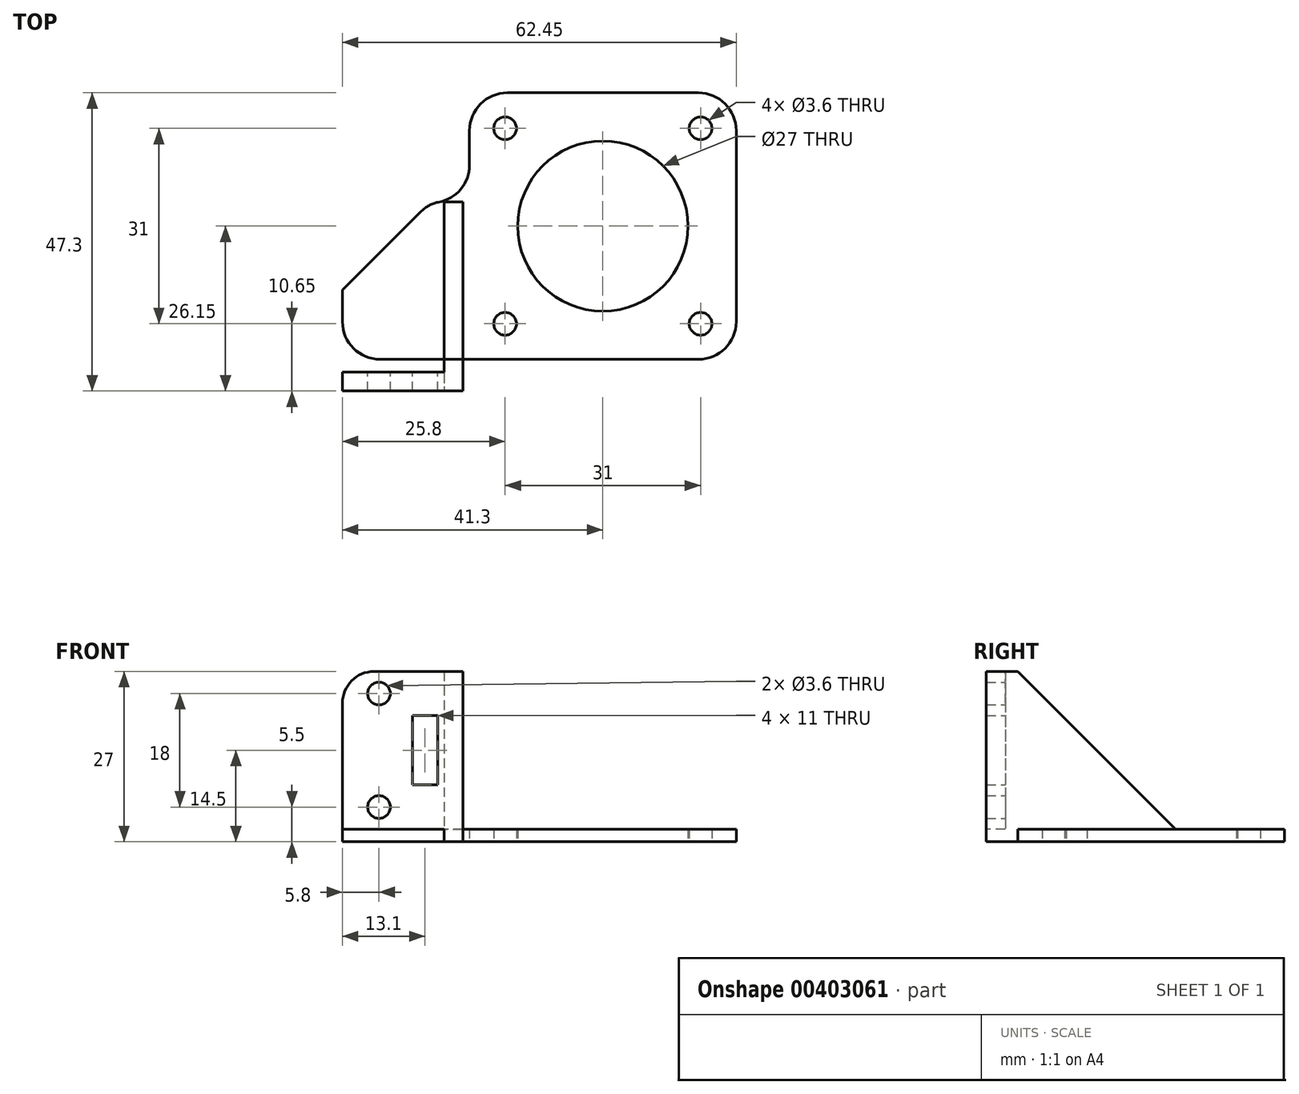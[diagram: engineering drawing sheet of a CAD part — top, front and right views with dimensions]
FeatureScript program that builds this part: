
annotation { "Feature Type Name" : "Feature", "Feature Type Description" : "" }
export const myFeature = defineFeature(function(context is Context, id is Id, definition is map)
    precondition{}
    {
        {
            var Q0;
            Q0=qCreatedBy(makeId("Top.planeOp"),FACE);
            var sketch = newSketch(context, id + "F0", { "sketchPlane" : qUnion([Q0])});
            skLineSegment(sketch, "E0.bottom", {"start": v(21.15, 21.15) * mm, "end": v(-21.15, 21.15) * mm});
            skLineSegment(sketch, "E0.top", {"start": v(21.15, -21.15) * mm, "end": v(-21.15, -21.15) * mm});
            skLineSegment(sketch, "E0.left", {"start": v(21.15, 21.15) * mm, "end": v(21.15, -21.15) * mm});
            skLineSegment(sketch, "E0.right", {"start": v(-21.15, 21.15) * mm, "end": v(-21.15, -21.15) * mm});
            skPoint(sketch, "E0.middle", {"position": v(0, 0) * mm});
            skLineSegment(sketch, "E1.bottom", {"start": v(15.5, 15.5) * mm, "end": v(-15.5, 15.5) * mm, "construction": true});
            skLineSegment(sketch, "E1.top", {"start": v(15.5, -15.5) * mm, "end": v(-15.5, -15.5) * mm, "construction": true});
            skLineSegment(sketch, "E1.left", {"start": v(15.5, 15.5) * mm, "end": v(15.5, -15.5) * mm, "construction": true});
            skLineSegment(sketch, "E1.right", {"start": v(-15.5, 15.5) * mm, "end": v(-15.5, -15.5) * mm, "construction": true});
            skCircle(sketch, "E2", {"center": v(-15.5, 15.5) * mm, "radius": 1.8 * mm});
            skCircle(sketch, "E3", {"center": v(15.5, 15.5) * mm, "radius": 1.8 * mm});
            skCircle(sketch, "E4", {"center": v(15.5, -15.5) * mm, "radius": 1.8 * mm});
            skCircle(sketch, "E5", {"center": v(-15.5, -15.5) * mm, "radius": 1.8 * mm});
            skCircle(sketch, "E6", {"center": v(0, 0) * mm, "radius": 13.5 * mm});
            skLineSegment(sketch, "E7.bottom", {"start": v(-21.15, -21.15) * mm, "end": v(-41.3, -21.15) * mm});
            skLineSegment(sketch, "E7.top", {"start": v(-21.15, 3.85) * mm, "end": v(-41.3, 3.85) * mm});
            skLineSegment(sketch, "E7.left", {"start": v(-21.15, -21.15) * mm, "end": v(-21.15, 3.85) * mm});
            skLineSegment(sketch, "E7.right", {"start": v(-41.3, -21.15) * mm, "end": v(-41.3, 3.85) * mm});
            skLineSegment(sketch, "E8.bottom", {"start": v(-41.3, -21.15) * mm, "end": v(-21.16, -21.15) * mm});
            skLineSegment(sketch, "E8.top", {"start": v(-41.3, -26.15) * mm, "end": v(-21.16, -26.15) * mm});
            skLineSegment(sketch, "E8.left", {"start": v(-41.3, -21.15) * mm, "end": v(-41.3, -26.15) * mm});
            skLineSegment(sketch, "E8.right", {"start": v(-21.16, -21.15) * mm, "end": v(-21.16, -26.15) * mm});
            skSolve(sketch);
        }
        {
            var Q0;
            Q0=makeQuery(id+"F0.imprint","IMPRINT",FACE,{"disambiguationData":[TD([[makeQuery(id+"F0.imprint","IMPRINT",EDGE,{"derivedFrom":sQuery(id+"F0.wireOp",EDGE,"E0.bottom")}),1.0]])]});
            var Q1;
            Q1=makeQuery(id+"F0.imprint","IMPRINT",FACE,{"disambiguationData":[TD([[makeQuery(id+"F0.imprint","IMPRINT",EDGE,{"derivedFrom":sQuery(id+"F0.wireOp",EDGE,"E7.bottom")}),-1.0]])]});
            var Q2;
            Q2=makeQuery(id+"F0.imprint","IMPRINT",FACE,{"disambiguationData":[TD([[makeQuery(id+"F0.imprint","IMPRINT",EDGE,{"derivedFrom":sQuery(id+"F0.wireOp",EDGE,"E8.bottom")}),-1.0]])]});
            extrude(context, id + "F1", {"entities" : qUnion([Q0, Q1, Q2]), "depth" : 2 * mm});
        }
        {
            var Q0;
            Q0=qCreatedBy(makeId("Top.planeOp"),FACE);
            var sketch = newSketch(context, id + "F2", { "sketchPlane" : qUnion([Q0])});
            skLineSegment(sketch, "E9.bottom", {"start": v(-22.16, 3.85) * mm, "end": v(-25.16, 3.85) * mm});
            skLineSegment(sketch, "E9.top", {"start": v(-22.16, -26.15) * mm, "end": v(-25.16, -26.15) * mm});
            skLineSegment(sketch, "E9.left", {"start": v(-22.16, 3.85) * mm, "end": v(-22.16, -26.15) * mm});
            skLineSegment(sketch, "E9.right", {"start": v(-25.16, 3.85) * mm, "end": v(-25.16, -26.15) * mm});
            skSolve(sketch);
        }
        {
            var Q0;
            Q0=qSketchRegion(id+"F2",true);
            extrude(context, id + "F3", {"entities" : qUnion([Q0]), "operationType" : NewBodyOperationType.ADD, "depth" : 27 * mm});
        }
        {
            var Q0;
            {var subQ0=sQuery(id+"F0.wireOp",EDGE,"E8.left");var subQ1=sQuery(id+"F0.wireOp",EDGE,"E7.right");var subQ2=sQuery(id+"F0.wireOp",EDGE,"E8.top");var subQ3=sQuery(id+"F0.wireOp",EDGE,"E7.top");Q0=makeQuery(id+"F3.boolean.opBoolean","SPLIT",FACE,{"disambiguationData":[TD([makeQuery(id+"F3.opExtrude","SWEPT_FACE",FACE,{"disambiguationData":[OSD([sQuery(id+"F2.wireOp",EDGE,"E9.right")])]})])],"derivedFrom":makeQuery(id+"F1.opExtrude","CAP_FACE",FACE,{"disambiguationData":[OSD([sQuery(id+"F0.wireOp",EDGE,"E0.bottom"),sQuery(id+"F0.wireOp",EDGE,"E0.top"),sQuery(id+"F0.wireOp",EDGE,"E0.left"),sQuery(id+"F0.wireOp",EDGE,"E0.right"),sQuery(id+"F0.wireOp",EDGE,"E2"),sQuery(id+"F0.wireOp",EDGE,"E3"),sQuery(id+"F0.wireOp",EDGE,"E4"),sQuery(id+"F0.wireOp",EDGE,"E5"),sQuery(id+"F0.wireOp",EDGE,"E6"),sQuery(id+"F0.wireOp",EDGE,"E7.bottom"),subQ3,subQ1,subQ2,subQ0,sQuery(id+"F0.wireOp",EDGE,"E8.right")])],"isStart":false})});}
            var sketch = newSketch(context, id + "F4", { "sketchPlane" : qUnion([Q0])});
            skLineSegment(sketch, "E10.bottom", {"start": v(-41.3, -23.15) * mm, "end": v(-25.16, -23.15) * mm});
            skLineSegment(sketch, "E10.top", {"start": v(-41.3, -26.15) * mm, "end": v(-25.16, -26.15) * mm});
            skLineSegment(sketch, "E10.left", {"start": v(-41.3, -23.15) * mm, "end": v(-41.3, -26.15) * mm});
            skLineSegment(sketch, "E10.right", {"start": v(-25.16, -23.15) * mm, "end": v(-25.16, -26.15) * mm});
            skSolve(sketch);
        }
        {
            var Q0;
            Q0=makeQuery(id+"F4.imprint","IMPRINT",FACE,{"disambiguationData":[TD([[makeQuery(id+"F4.imprint","IMPRINT",EDGE,{"derivedFrom":sQuery(id+"F4.wireOp",EDGE,"E10.bottom")}),-1.0]])]});
            extrude(context, id + "F5", {"entities" : qUnion([Q0]), "operationType" : NewBodyOperationType.ADD, "depth" : 25 * mm});
        }
        {
            var Q0;
            Q0=makeQuery(id+"F5.opExtrude","SWEPT_FACE",FACE,{"disambiguationData":[OSD([sQuery(id+"F4.wireOp",EDGE,"E10.bottom")])]});
            var sketch = newSketch(context, id + "F6", { "sketchPlane" : qUnion([Q0])});
            skCircle(sketch, "E11", {"center": v(35.5, 5.5) * mm, "radius": 1.8 * mm});
            skCircle(sketch, "E12", {"center": v(35.5, 23.5) * mm, "radius": 1.8 * mm});
            skLineSegment(sketch, "E13.bottom", {"start": v(30.2, 20) * mm, "end": v(26.2, 20) * mm});
            skLineSegment(sketch, "E13.top", {"start": v(30.2, 9) * mm, "end": v(26.2, 9) * mm});
            skLineSegment(sketch, "E13.left", {"start": v(30.2, 20) * mm, "end": v(30.2, 9) * mm});
            skLineSegment(sketch, "E13.right", {"start": v(26.2, 20) * mm, "end": v(26.2, 9) * mm});
            skSolve(sketch);
        }
        {
            var Q0;
            Q0=makeQuery(id+"F6.imprint","IMPRINT",FACE,{"disambiguationData":[TD([[makeQuery(id+"F6.imprint","IMPRINT",EDGE,{"derivedFrom":sQuery(id+"F6.wireOp",EDGE,"8oqH9Klm-JO6Q-5Q7F-NUQf-TBMxwuCzCkZV")}),1.0]])]});
            var Q1;
            Q1=makeQuery(id+"F6.imprint","IMPRINT",FACE,{"disambiguationData":[TD([[makeQuery(id+"F6.imprint","IMPRINT",EDGE,{"derivedFrom":sQuery(id+"F6.wireOp",EDGE,"E11")}),1.0]])]});
            var Q2;
            Q2=makeQuery(id+"F6.imprint","IMPRINT",FACE,{"disambiguationData":[TD([[makeQuery(id+"F6.imprint","IMPRINT",EDGE,{"derivedFrom":sQuery(id+"F6.wireOp",EDGE,"E12")}),1.0]])]});
            var Q3;
            Q3=makeQuery(id+"F6.imprint","IMPRINT",FACE,{"disambiguationData":[TD([[makeQuery(id+"F6.imprint","IMPRINT",EDGE,{"derivedFrom":sQuery(id+"F6.wireOp",EDGE,"E13.bottom")}),1.0]])]});
            extrude(context, id + "F7", {"entities" : qUnion([Q0, Q1, Q2, Q3]), "operationType" : NewBodyOperationType.REMOVE, "oppositeDirection" : true, "depth" : 25 * mm});
        }
        {
            var Q0;
            Q0=makeQuery(id+"F3.opExtrude","CAP_EDGE",EDGE,{"disambiguationData":[OSD([sQuery(id+"F2.wireOp",EDGE,"E9.bottom")])],"isStart":false});
            chamfer(context, id + "F8", {"entities" : qUnion([Q0]), "width" : 25 * mm, "tangentPropagation" : true});
        }
        {
            var Q0;
            Q0=makeQuery(id+"F1.opExtrude","SWEPT_EDGE",EDGE,{"disambiguationData":[OSD([sQuery(id+"F0.wireOp",EDGE,"E7.top"),sQuery(id+"F0.wireOp",EDGE,"E7.right")])]});
            chamfer(context, id + "F9", {"entities" : qUnion([Q0]), "width" : 14 * mm, "tangentPropagation" : true});
        }
        {
            var Q0;
            {var subQ0=sQuery(id+"F0.wireOp",EDGE,"E7.right");Q0=makeQuery(id+"F9.opChamfer","BLEND_EDGE",EDGE,{"blendedFrom":[makeQuery(id+"F1.opExtrude","SWEPT_EDGE",EDGE,{"disambiguationData":[OSD([sQuery(id+"F0.wireOp",EDGE,"E7.top"),subQ0])]}),makeQuery(id+"F5.boolean.opBoolean","MERGE",FACE,{"derivedFrom":[makeQuery(id+"F1.opExtrude","SWEPT_FACE",FACE,{"disambiguationData":[OSD([subQ0,sQuery(id+"F0.wireOp",EDGE,"E8.left")])]}),makeQuery(id+"F5.opExtrude","SWEPT_FACE",FACE,{"disambiguationData":[OSD([sQuery(id+"F4.wireOp",EDGE,"E10.left")])]})]})],"blendedInto":[makeQuery(id+"F5.boolean.opBoolean","MERGE",FACE,{"derivedFrom":[makeQuery(id+"F1.opExtrude","SWEPT_FACE",FACE,{"disambiguationData":[OSD([subQ0,sQuery(id+"F0.wireOp",EDGE,"E8.left")])]}),makeQuery(id+"F5.opExtrude","SWEPT_FACE",FACE,{"disambiguationData":[OSD([sQuery(id+"F4.wireOp",EDGE,"E10.left")])]})]})]});}
            var Q1;
            {var subQ0=sQuery(id+"F0.wireOp",EDGE,"E7.top");Q1=makeQuery(id+"F9.opChamfer","BLEND_EDGE",EDGE,{"blendedFrom":[makeQuery(id+"F1.opExtrude","SWEPT_EDGE",EDGE,{"disambiguationData":[OSD([subQ0,sQuery(id+"F0.wireOp",EDGE,"E7.right")])]}),makeQuery(id+"F3.boolean.opBoolean","MERGE",FACE,{"derivedFrom":[makeQuery(id+"F1.opExtrude","SWEPT_FACE",FACE,{"disambiguationData":[OSD([subQ0])]}),makeQuery(id+"F3.opExtrude","SWEPT_FACE",FACE,{"disambiguationData":[OSD([sQuery(id+"F2.wireOp",EDGE,"E9.bottom")])]})]})],"blendedInto":[makeQuery(id+"F3.boolean.opBoolean","MERGE",FACE,{"derivedFrom":[makeQuery(id+"F1.opExtrude","SWEPT_FACE",FACE,{"disambiguationData":[OSD([subQ0])]}),makeQuery(id+"F3.opExtrude","SWEPT_FACE",FACE,{"disambiguationData":[OSD([sQuery(id+"F2.wireOp",EDGE,"E9.bottom")])]})]})]});}
            var Q2;
            Q2=makeQuery(id+"F1.opExtrude","SWEPT_EDGE",EDGE,{"disambiguationData":[OSD([sQuery(id+"F0.wireOp",EDGE,"E8.top"),sQuery(id+"F0.wireOp",EDGE,"E8.right")])]});
            var Q3;
            Q3=makeQuery(id+"F5.opExtrude","CAP_EDGE",EDGE,{"disambiguationData":[OSD([sQuery(id+"F4.wireOp",EDGE,"E10.left")])],"isStart":false});
            fillet(context, id + "F10", {"entities" : qUnion([Q0, Q1, Q2, Q3]), "radius" : 5 * mm, "tangentPropagation" : true, "allowEdgeOverflow" : false});
        }
        {
            var Q0;
            Q0=makeQuery(id+"F1.opExtrude","SWEPT_EDGE",EDGE,{"disambiguationData":[OSD([sQuery(id+"F0.wireOp",EDGE,"E0.top"),sQuery(id+"F0.wireOp",EDGE,"E0.left")])]});
            var Q1;
            Q1=makeQuery(id+"F1.opExtrude","SWEPT_EDGE",EDGE,{"disambiguationData":[OSD([sQuery(id+"F0.wireOp",EDGE,"E0.bottom"),sQuery(id+"F0.wireOp",EDGE,"E0.left")])]});
            var Q2;
            Q2=makeQuery(id+"F1.opExtrude","SWEPT_EDGE",EDGE,{"disambiguationData":[OSD([sQuery(id+"F0.wireOp",EDGE,"E0.bottom"),sQuery(id+"F0.wireOp",EDGE,"E0.right")])]});
            var Q3;
            Q3=makeQuery(id+"F1.opExtrude","SWEPT_EDGE",EDGE,{"disambiguationData":[OSD([sQuery(id+"F0.wireOp",EDGE,"E0.right"),sQuery(id+"F0.wireOp",EDGE,"E7.top"),sQuery(id+"F0.wireOp",EDGE,"E7.left")])]});
            var Q4;
            Q4=makeQuery(id+"F1.opExtrude","SWEPT_EDGE",EDGE,{"disambiguationData":[OSD([sQuery(id+"F0.wireOp",EDGE,"E7.bottom"),sQuery(id+"F0.wireOp",EDGE,"E8.bottom"),sQuery(id+"F0.wireOp",EDGE,"E8.right")])]});
            fillet(context, id + "F11", {"entities" : qUnion([Q0, Q1, Q2, Q3, Q4]), "radius" : 6 * mm, "tangentPropagation" : true, "allowEdgeOverflow" : false});
        }
    });
